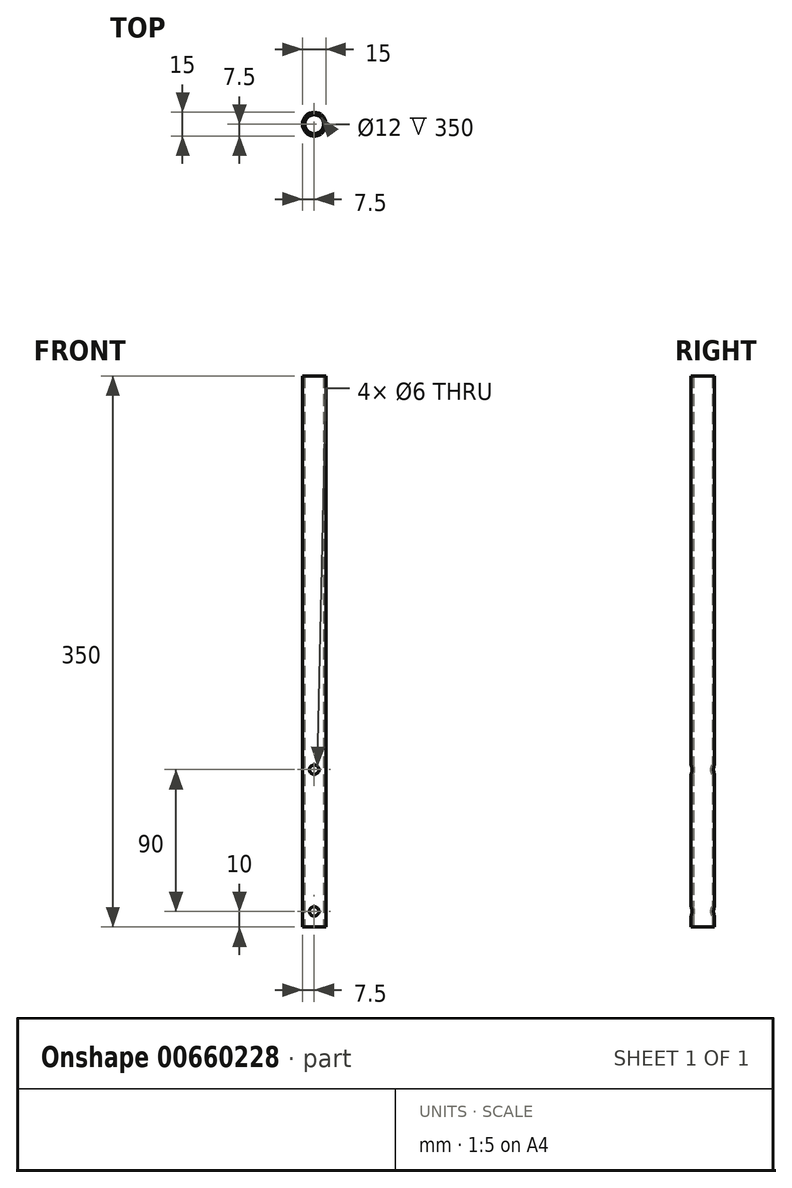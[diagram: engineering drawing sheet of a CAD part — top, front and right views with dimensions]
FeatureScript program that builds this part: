
annotation { "Feature Type Name" : "Feature", "Feature Type Description" : "" }
export const myFeature = defineFeature(function(context is Context, id is Id, definition is map)
    precondition{}
    {
        {
            var Q0;
            Q0=qCreatedBy(makeId("Top.planeOp"),FACE);
            var sketch = newSketch(context, id + "F0", { "sketchPlane" : qUnion([Q0])});
            skCircle(sketch, "E0", {"center": v(0, 0) * mm, "radius": 7.5 * mm});
            skCircle(sketch, "E1", {"center": v(0, 0) * mm, "radius": 6 * mm});
            skSolve(sketch);
        }
        {
            var Q0;
            Q0 = qSketchRegion(id + "F0", true);
            extrude(context, id + "F1", {"entities" : qUnion([Q0]), "depth" : 350 * mm, "offsetDistance" : 25 * mm});
        }
        {
            var Q0;
            Q0=qCreatedBy(makeId("Front.planeOp"),FACE);
            var sketch = newSketch(context, id + "F2", { "sketchPlane" : qUnion([Q0])});
            skCircle(sketch, "E2", {"center": v(0, 100) * mm, "radius": 3 * mm});
            skCircle(sketch, "E3", {"center": v(0, 10) * mm, "radius": 3 * mm});
            skSolve(sketch);
        }
        {
            var Q0;
            Q0 = qSketchRegion(id + "F2", true);
            extrude(context, id + "F3", {"entities" : qUnion([Q0]), "operationType" : NewBodyOperationType.REMOVE, "endBound" : BoundingType.SYMMETRIC, "oppositeDirection" : true, "depth" : 25 * mm, "offsetDistance" : 25 * mm});
        }
    });
